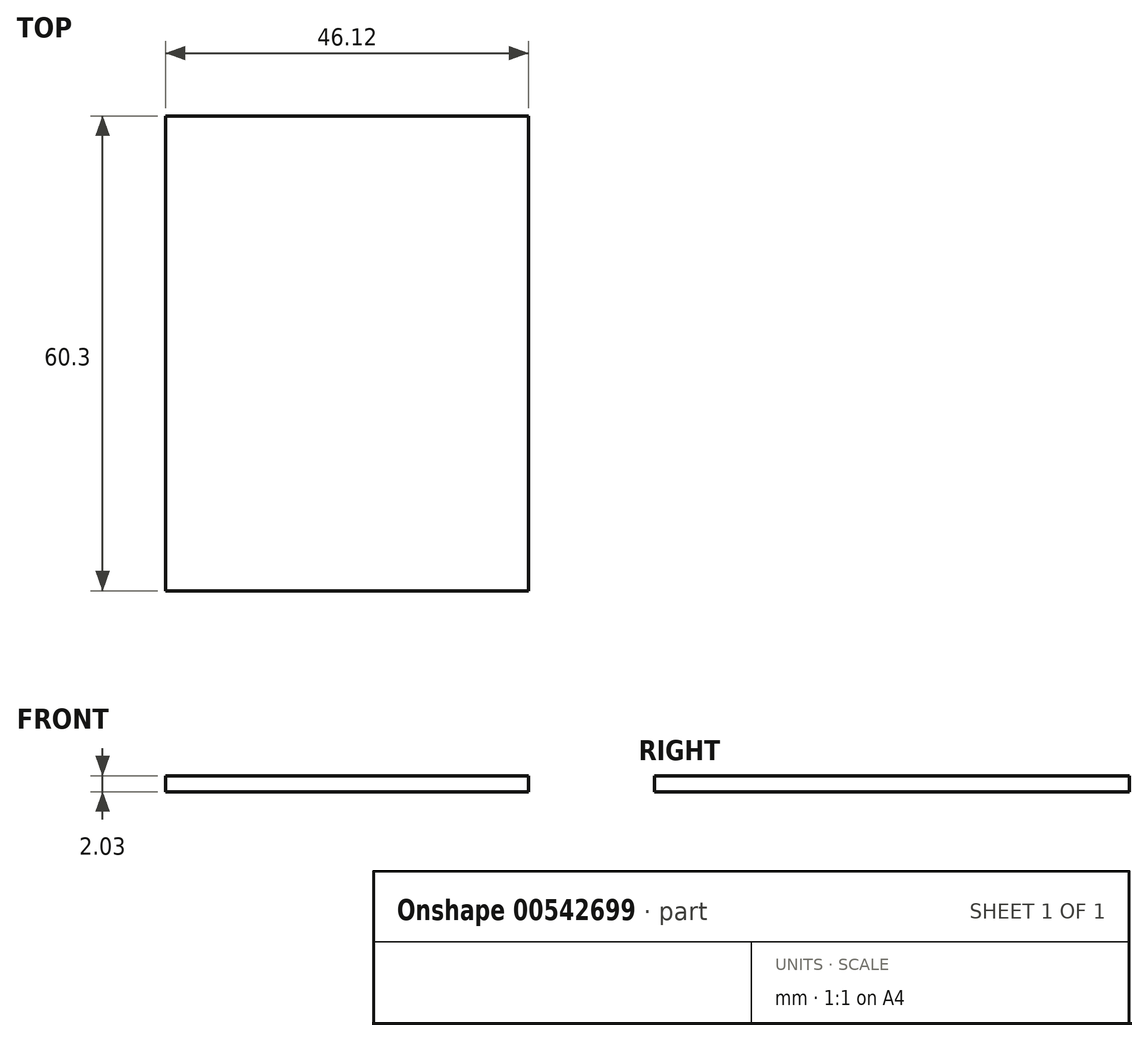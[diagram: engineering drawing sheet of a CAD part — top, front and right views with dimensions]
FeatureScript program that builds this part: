
annotation { "Feature Type Name" : "Feature", "Feature Type Description" : "" }
export const myFeature = defineFeature(function(context is Context, id is Id, definition is map)
    precondition{}
    {
        {
            var Q0;
            Q0=qCreatedBy(makeId("Top.planeOp"),FACE);
            var sketch = newSketch(context, id + "F0", { "sketchPlane" : qUnion([Q0])});
            skLineSegment(sketch, "E0.bottom", {"start": v(23.06, 30.15) * mm, "end": v(-23.06, 30.15) * mm});
            skLineSegment(sketch, "E0.top", {"start": v(23.06, -30.15) * mm, "end": v(-23.06, -30.15) * mm});
            skLineSegment(sketch, "E0.left", {"start": v(23.06, 30.15) * mm, "end": v(23.06, -30.15) * mm});
            skLineSegment(sketch, "E0.right", {"start": v(-23.06, 30.15) * mm, "end": v(-23.06, -30.15) * mm});
            skPoint(sketch, "E0.middle", {"position": v(0, 0) * mm});
            skSolve(sketch);
        }
        {
            var Q0;
            Q0 = qSketchRegion(id + "F0", true);
            extrude(context, id + "F1", {"entities" : qUnion([Q0]), "depth" : 2.03 * mm, "offsetDistance" : 25.4 * mm});
        }
    });
